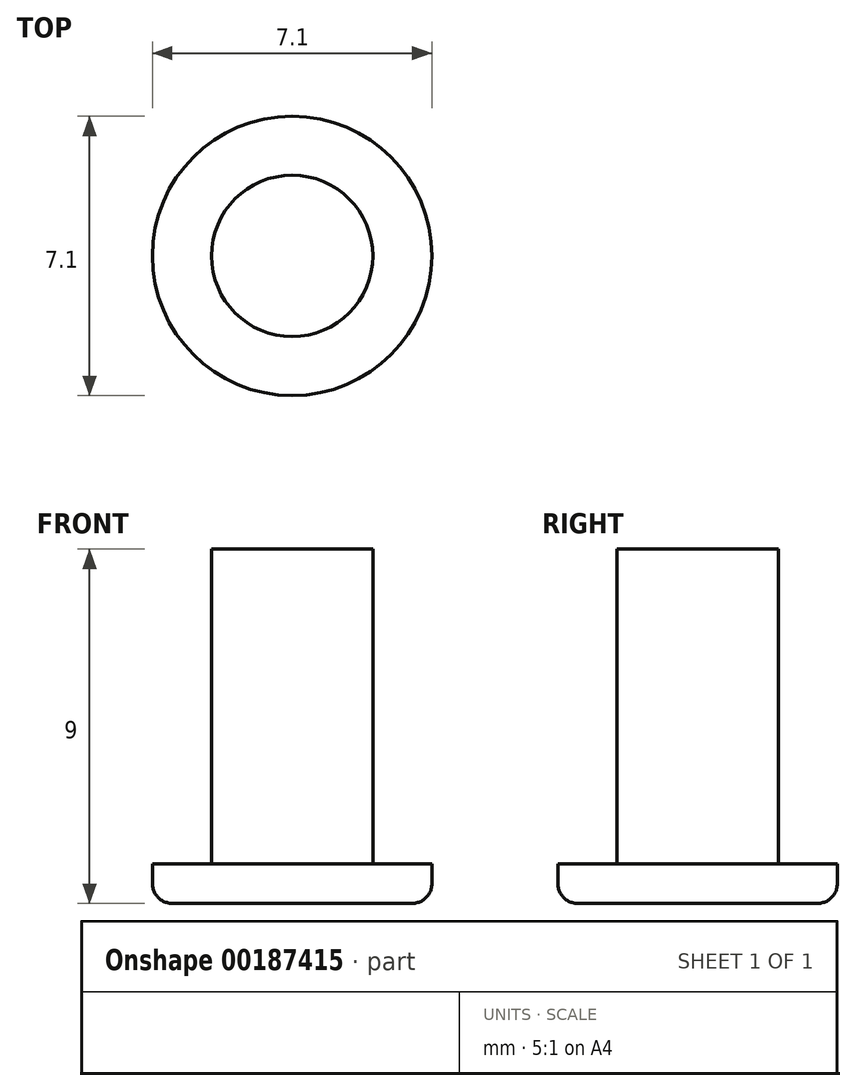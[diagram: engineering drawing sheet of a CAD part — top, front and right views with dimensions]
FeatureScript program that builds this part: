
annotation { "Feature Type Name" : "Feature", "Feature Type Description" : "" }
export const myFeature = defineFeature(function(context is Context, id is Id, definition is map)
    precondition{}
    {
        {
            var Q0;
            Q0=qCreatedBy(makeId("Top.planeOp"),FACE);
            var sketch = newSketch(context, id + "F0", { "sketchPlane" : qUnion([Q0])});
            skCircle(sketch, "E0", {"center": v(0, 0) * mm, "radius": 2.05 * mm});
            skSolve(sketch);
        }
        {
            var Q0;
            Q0=makeQuery(id+"F0.imprint","IMPRINT",FACE,{"disambiguationData":[TD([[makeQuery(id+"F0.imprint","IMPRINT",EDGE,{"derivedFrom":sQuery(id+"F0.wireOp",EDGE,"E0")}),1.0]])]});
            extrude(context, id + "F1", {"entities" : qUnion([Q0]), "depth" : 8 * mm});
        }
        {
            var Q0;
            Q0=makeQuery(id+"F1.opExtrude","CAP_FACE",FACE,{"disambiguationData":[OSD([sQuery(id+"F0.wireOp",EDGE,"E0")])],"isStart":true});
            var sketch = newSketch(context, id + "F2", { "sketchPlane" : qUnion([Q0])});
            skCircle(sketch, "E1", {"center": v(0, 0) * mm, "radius": 3.55 * mm});
            skSolve(sketch);
        }
        {
            var Q0;
            Q0=makeQuery(id+"F2.imprint","IMPRINT",FACE,{"disambiguationData":[TD([[makeQuery(id+"F2.imprint","IMPRINT",EDGE,{"derivedFrom":sQuery(id+"F2.wireOp",EDGE,"E1")}),1.0]])]});
            var Q1;
            Q1=makeQuery(id+"F2.imprint","IMPRINT",FACE,{"disambiguationData":[TD([[makeQuery(id+"F2.imprint","IMPRINT",EDGE,{"derivedFrom":makeQuery(id+"F1.opExtrude","CAP_EDGE",EDGE,{"disambiguationData":[OSD([sQuery(id+"F0.wireOp",EDGE,"E0")])],"isStart":true})}),-1.0]])]});
            extrude(context, id + "F3", {"entities" : qUnion([Q0, Q1]), "operationType" : NewBodyOperationType.ADD, "depth" : 1 * mm});
        }
        {
            var Q0;
            Q0=makeQuery(id+"F3.opExtrude","CAP_EDGE",EDGE,{"disambiguationData":[OSD([sQuery(id+"F2.wireOp",EDGE,"E1")])],"isStart":false});
            fillet(context, id + "F4", {"entities" : qUnion([Q0]), "radius" : .5 * mm, "tangentPropagation" : true, "allowEdgeOverflow" : false});
        }
    });
